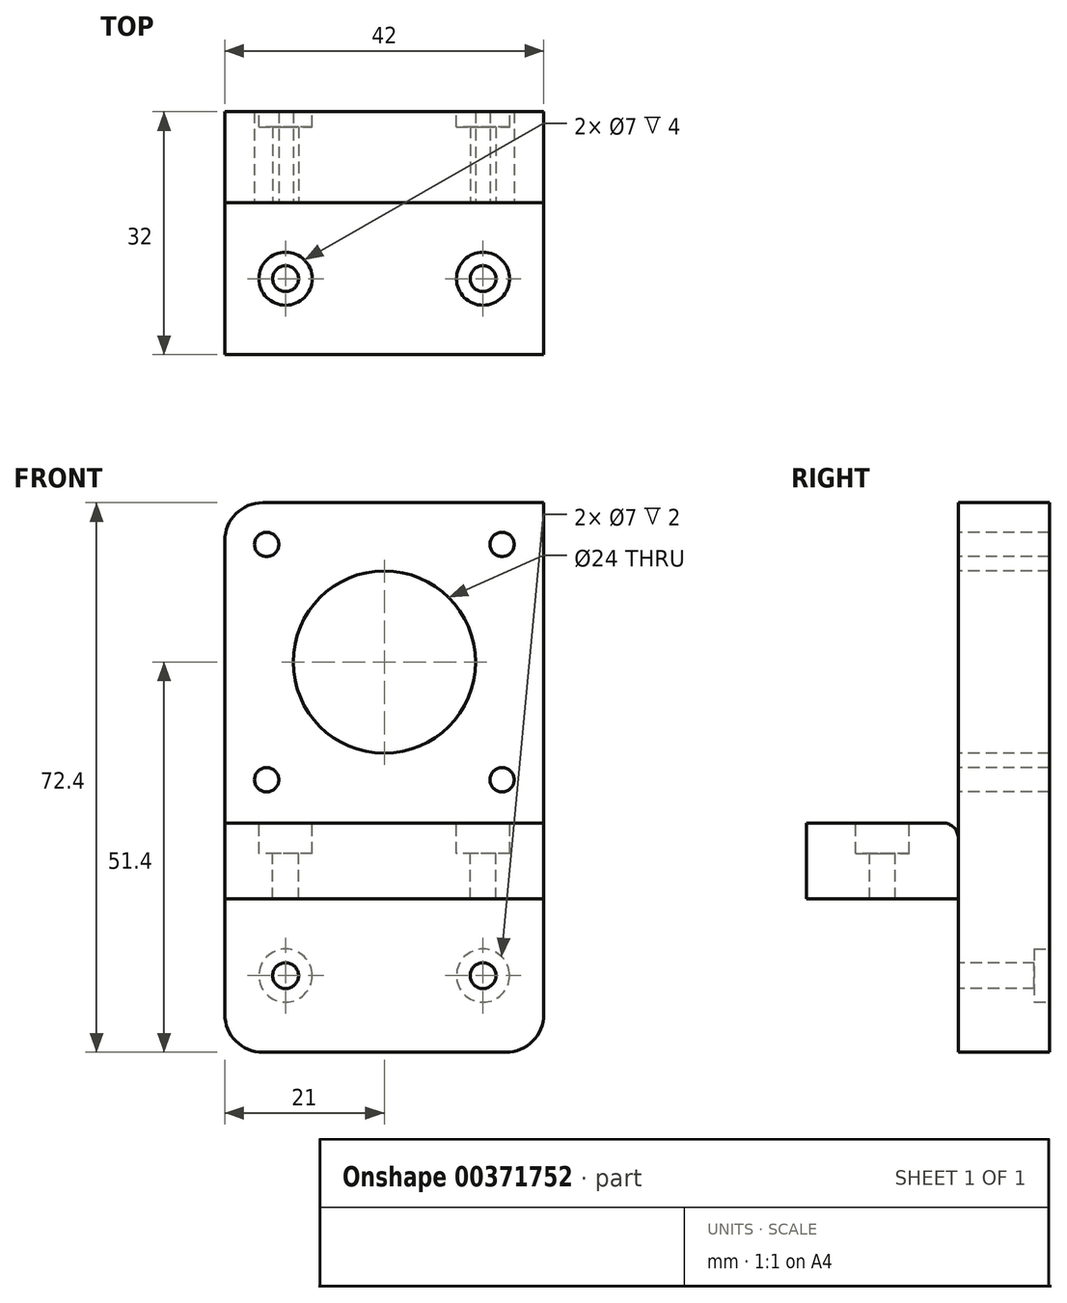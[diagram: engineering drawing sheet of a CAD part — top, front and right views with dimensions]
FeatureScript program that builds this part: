
annotation { "Feature Type Name" : "Feature", "Feature Type Description" : "" }
export const myFeature = defineFeature(function(context is Context, id is Id, definition is map)
    precondition{}
    {
        {
            var Q0;
            Q0=qCreatedBy(makeId("Front.planeOp"),FACE);
            var sketch = newSketch(context, id + "F0", { "sketchPlane" : qUnion([Q0])});
            skLineSegment(sketch, "E0.bottom", {"start": v(-21, 21) * mm, "end": v(21, 21) * mm});
            skLineSegment(sketch, "E0.left", {"start": v(-21, 21) * mm, "end": v(-21, -21) * mm});
            skLineSegment(sketch, "E0.right", {"start": v(21, 21) * mm, "end": v(21, -21) * mm});
            skPoint(sketch, "E0.middle", {"position": v(0, 0) * mm});
            skLineSegment(sketch, "E1", {"start": v(0, 0) * mm, "end": v(15.5, 0) * mm, "construction": true});
            skLineSegment(sketch, "E2", {"start": v(0, 0) * mm, "end": v(0, 15.5) * mm, "construction": true});
            skLineSegment(sketch, "E3", {"start": v(15.5, -21) * mm, "end": v(15.5, 21) * mm, "construction": true});
            skLineSegment(sketch, "E4", {"start": v(21, 15.5) * mm, "end": v(-21, 15.5) * mm, "construction": true});
            skLineSegment(sketch, "E5", {"start": v(0, 0) * mm, "end": v(-15.5, 0) * mm, "construction": true});
            skLineSegment(sketch, "E6", {"start": v(0, 0) * mm, "end": v(0, -15.5) * mm, "construction": true});
            skLineSegment(sketch, "E7", {"start": v(-15.5, 21) * mm, "end": v(-15.5, -21) * mm, "construction": true});
            skLineSegment(sketch, "E8", {"start": v(21, -15.5) * mm, "end": v(-21, -15.5) * mm, "construction": true});
            skCircle(sketch, "E9", {"center": v(-15.5, 15.5) * mm, "radius": 1.6 * mm});
            skCircle(sketch, "E10", {"center": v(15.5, 15.5) * mm, "radius": 1.6 * mm});
            skCircle(sketch, "E11", {"center": v(15.5, -15.5) * mm, "radius": 1.6 * mm});
            skCircle(sketch, "E12", {"center": v(-15.5, -15.5) * mm, "radius": 1.6 * mm});
            skLineSegment(sketch, "E13", {"start": v(-21, -21) * mm, "end": v(21, -21) * mm});
            skLineSegment(sketch, "E14.0", {"start": v(-21, -21.2) * mm, "end": v(21, -21.2) * mm});
            skLineSegment(sketch, "E15", {"start": v(21, -21.2) * mm, "end": v(21, -31.2) * mm});
            skLineSegment(sketch, "E16", {"start": v(-21, -31.2) * mm, "end": v(21, -31.2) * mm});
            skLineSegment(sketch, "E17.bottom", {"start": v(-21.2, 21) * mm, "end": v(21, 21) * mm});
            skLineSegment(sketch, "E17.right", {"start": v(21, 21) * mm, "end": v(21, -31.2) * mm});
            skCircle(sketch, "E18", {"center": v(0, 0) * mm, "radius": 12 * mm});
            skLineSegment(sketch, "E19.top", {"start": v(21, -51.4) * mm, "end": v(-21, -51.4) * mm});
            skLineSegment(sketch, "E19.left", {"start": v(21, -31.2) * mm, "end": v(21, -51.4) * mm});
            skLineSegment(sketch, "E20", {"start": v(21, -31.2) * mm, "end": v(21, -31.4) * mm, "construction": true});
            skLineSegment(sketch, "E21", {"start": v(21, -31.4) * mm, "end": v(-21, -31.4) * mm, "construction": true});
            skLineSegment(sketch, "E22", {"start": v(0, -41.3) * mm, "end": v(13, -41.3) * mm, "construction": true});
            skPoint(sketch, "E22.startSnap0", {"position": v(21, -41.3) * mm});
            skLineSegment(sketch, "E23", {"start": v(0, -41.3) * mm, "end": v(-13, -41.3) * mm, "construction": true});
            skCircle(sketch, "E24", {"center": v(13, -41.3) * mm, "radius": 1.7 * mm});
            skCircle(sketch, "E25", {"center": v(-13, -41.3) * mm, "radius": 1.7 * mm});
            skCircle(sketch, "E26", {"center": v(13, -41.3) * mm, "radius": 3.5 * mm});
            skCircle(sketch, "E27", {"center": v(-13, -41.3) * mm, "radius": 3.5 * mm});
            skLineSegment(sketch, "E28", {"start": v(-21, -21) * mm, "end": v(-21, -51.4) * mm});
            skSolve(sketch);
        }
        {
            var Q0;
            {var subQ4=sQuery(id+"F0.wireOp",EDGE,"E14.0");Q0=makeQuery(id+"F0.imprint","IMPRINT",FACE,{"disambiguationData":[TD([[makeQuery(id+"F0.imprint","IMPRINT",EDGE,{"derivedFrom":subQ4}),-1.0]])]});}
            extrude(context, id + "F1", {"entities" : qUnion([Q0]), "depth" : 20 * mm});
        }
        {
            var Q0;
            {var subQ3=sQuery(id+"F0.wireOp",EDGE,"E0.left");Q0=makeQuery(id+"F0.imprint","IMPRINT",FACE,{"disambiguationData":[TD([[makeQuery(id+"F0.imprint","IMPRINT",EDGE,{"derivedFrom":subQ3}),-1.0]])]});}
            var Q1;
            {var subQ4=sQuery(id+"F0.wireOp",EDGE,"E14.0");Q1=makeQuery(id+"F0.imprint","IMPRINT",FACE,{"disambiguationData":[TD([[makeQuery(id+"F0.imprint","IMPRINT",EDGE,{"derivedFrom":subQ4}),-1.0]])]});}
            var Q2;
            {var subQ4=sQuery(id+"F0.wireOp",EDGE,"E0.left");Q2=makeQuery(id+"F0.imprint","IMPRINT",FACE,{"disambiguationData":[TD([[makeQuery(id+"F0.imprint","IMPRINT",EDGE,{"derivedFrom":subQ4}),1.0]])]});}
            var Q3;
            {var subQ1=sQuery(id+"F0.wireOp",EDGE,"E16");Q3=makeQuery(id+"F0.imprint","IMPRINT",FACE,{"disambiguationData":[TD([[makeQuery(id+"F0.imprint","IMPRINT",EDGE,{"derivedFrom":subQ1}),-1.0]])]});}
            var Q4;
            {var subQ0=sQuery(id+"F0.wireOp",EDGE,"E13");Q4=makeQuery(id+"F0.imprint","IMPRINT",FACE,{"disambiguationData":[TD([[makeQuery(id+"F0.imprint","IMPRINT",EDGE,{"derivedFrom":subQ0}),-1.0]])]});}
            extrude(context, id + "F2", {"entities" : qUnion([Q0, Q1, Q2, Q3, Q4]), "oppositeDirection" : true, "depth" : 12 * mm});
        }
        {
            var Q0;
            Q0=makeQuery(id+"F1.opExtrude","SWEPT_FACE",FACE,{"disambiguationData":[OSD([sQuery(id+"F0.wireOp",EDGE,"E14.0")])]});
            var sketch = newSketch(context, id + "F3", { "sketchPlane" : qUnion([Q0])});
            skLineSegment(sketch, "E29", {"start": v(0, 0) * mm, "end": v(0, -20) * mm, "construction": true});
            skLineSegment(sketch, "E30", {"start": v(0, -10) * mm, "end": v(13, -10) * mm, "construction": true});
            skPoint(sketch, "E30.endSnap0", {"position": v(0, -10) * mm});
            skLineSegment(sketch, "E31", {"start": v(0, -10) * mm, "end": v(-13, -10) * mm, "construction": true});
            skCircle(sketch, "E32", {"center": v(-13, -10) * mm, "radius": 1.7 * mm});
            skCircle(sketch, "E33", {"center": v(13, -10) * mm, "radius": 1.7 * mm});
            skCircle(sketch, "E34", {"center": v(-13, -10) * mm, "radius": 3.5 * mm});
            skCircle(sketch, "E35", {"center": v(13, -10) * mm, "radius": 3.5 * mm});
            skSolve(sketch);
        }
        {
            var Q0;
            Q0=makeQuery(id+"F3.imprint","IMPRINT",FACE,{"disambiguationData":[TD([[makeQuery(id+"F3.imprint","IMPRINT",EDGE,{"derivedFrom":sQuery(id+"F3.wireOp",EDGE,"E32")}),1.0]])]});
            var Q1;
            Q1=makeQuery(id+"F3.imprint","IMPRINT",FACE,{"disambiguationData":[TD([[makeQuery(id+"F3.imprint","IMPRINT",EDGE,{"derivedFrom":sQuery(id+"F3.wireOp",EDGE,"E33")}),1.0]])]});
            extrude(context, id + "F4", {"entities" : qUnion([Q0, Q1]), "operationType" : NewBodyOperationType.REMOVE, "oppositeDirection" : true, "depth" : 25 * mm});
        }
        {
            var Q0;
            Q0=makeQuery(id+"F3.imprint","IMPRINT",FACE,{"disambiguationData":[TD([[makeQuery(id+"F3.imprint","IMPRINT",EDGE,{"derivedFrom":sQuery(id+"F3.wireOp",EDGE,"E32")}),-1.0]])]});
            var Q1;
            Q1=makeQuery(id+"F3.imprint","IMPRINT",FACE,{"disambiguationData":[TD([[makeQuery(id+"F3.imprint","IMPRINT",EDGE,{"derivedFrom":sQuery(id+"F3.wireOp",EDGE,"E33")}),-1.0]])]});
            extrude(context, id + "F5", {"entities" : qUnion([Q0, Q1]), "operationType" : NewBodyOperationType.REMOVE, "oppositeDirection" : true, "depth" : 4 * mm});
        }
        {
            var Q0;
            Q0=makeQuery(id+"F0.imprint","IMPRINT",FACE,{"disambiguationData":[TD([[makeQuery(id+"F0.imprint","IMPRINT",EDGE,{"derivedFrom":sQuery(id+"F0.wireOp",EDGE,"E19.bottom")}),1.0]])]});
            var Q1;
            Q1=makeQuery(id+"F0.imprint","IMPRINT",FACE,{"disambiguationData":[TD([[makeQuery(id+"F0.imprint","IMPRINT",EDGE,{"derivedFrom":sQuery(id+"F0.wireOp",EDGE,"E24")}),-1.0]])]});
            var Q2;
            Q2=makeQuery(id+"F0.imprint","IMPRINT",FACE,{"disambiguationData":[TD([[makeQuery(id+"F0.imprint","IMPRINT",EDGE,{"derivedFrom":sQuery(id+"F0.wireOp",EDGE,"E25")}),-1.0]])]});
            extrude(context, id + "F6", {"entities" : qUnion([Q0, Q1, Q2]), "operationType" : NewBodyOperationType.ADD, "oppositeDirection" : true, "depth" : 12 * mm});
        }
        {
            var Q0;
            {var subQ0=sQuery(id+"F0.wireOp",EDGE,"E19.bottom");Q0=makeQuery(id+"F6.boolean.opBoolean","MERGE",FACE,{"derivedFrom":[makeQuery(id+"F2.opExtrude","CAP_FACE",FACE,{"disambiguationData":[OSD([sQuery(id+"F0.wireOp",EDGE,"E9"),sQuery(id+"F0.wireOp",EDGE,"E10"),sQuery(id+"F0.wireOp",EDGE,"E11"),sQuery(id+"F0.wireOp",EDGE,"E12"),sQuery(id+"F0.wireOp",EDGE,"E17.bottom"),sQuery(id+"F0.wireOp",EDGE,"E17.top"),sQuery(id+"F0.wireOp",EDGE,"E17.left"),sQuery(id+"F0.wireOp",EDGE,"E17.right"),sQuery(id+"F0.wireOp",EDGE,"E18"),subQ0])],"isStart":false}),makeQuery(id+"F6.opExtrude","CAP_FACE",FACE,{"disambiguationData":[OSD([subQ0,sQuery(id+"F0.wireOp",EDGE,"E19.top"),sQuery(id+"F0.wireOp",EDGE,"E19.left"),sQuery(id+"F0.wireOp",EDGE,"E19.right"),sQuery(id+"F0.wireOp",EDGE,"E24"),sQuery(id+"F0.wireOp",EDGE,"E25")])],"isStart":false})]});}
            var sketch = newSketch(context, id + "F7", { "sketchPlane" : qUnion([Q0])});
            skCircle(sketch, "E36", {"center": v(-13, -41.3) * mm, "radius": 3.5 * mm});
            skCircle(sketch, "E37", {"center": v(13, -41.3) * mm, "radius": 3.5 * mm});
            skSolve(sketch);
        }
        {
            var Q0;
            Q0=makeQuery(id+"F7.imprint","IMPRINT",FACE,{"disambiguationData":[TD([[makeQuery(id+"F7.imprint","IMPRINT",EDGE,{"derivedFrom":sQuery(id+"F7.wireOp",EDGE,"E36")}),1.0]])]});
            var Q1;
            Q1=makeQuery(id+"F7.imprint","IMPRINT",FACE,{"disambiguationData":[TD([[makeQuery(id+"F7.imprint","IMPRINT",EDGE,{"derivedFrom":sQuery(id+"F7.wireOp",EDGE,"E37")}),1.0]])]});
            extrude(context, id + "F8", {"entities" : qUnion([Q0, Q1]), "operationType" : NewBodyOperationType.REMOVE, "oppositeDirection" : true, "depth" : 2 * mm});
        }
        {
            var Q0;
            Q0=makeQuery(id+"F2.opExtrude","SWEPT_EDGE",EDGE,{"disambiguationData":[OSD([sQuery(id+"F0.wireOp",EDGE,"E17.bottom"),sQuery(id+"F0.wireOp",EDGE,"E17.right")])]});
            var Q1;
            Q1=makeQuery(id+"F2.opExtrude","SWEPT_EDGE",EDGE,{"disambiguationData":[OSD([sQuery(id+"F0.wireOp",EDGE,"E0.left"),sQuery(id+"F0.wireOp",EDGE,"E17.bottom")])]});
            var Q2;
            Q2=makeQuery(id+"F2.opExtrude","SWEPT_EDGE",EDGE,{"disambiguationData":[OSD([sQuery(id+"F0.wireOp",EDGE,"E19.top"),sQuery(id+"F0.wireOp",EDGE,"E28")])]});
            var Q3;
            Q3=makeQuery(id+"F2.opExtrude","SWEPT_EDGE",EDGE,{"disambiguationData":[OSD([sQuery(id+"F0.wireOp",EDGE,"E19.top"),sQuery(id+"F0.wireOp",EDGE,"E19.left")])]});
            fillet(context, id + "F9", {"entities" : qUnion([Q0, Q1, Q2, Q3]), "radius" : 5 * mm, "tangentPropagation" : true, "allowEdgeOverflow" : false});
        }
        {
            var Q0;
            Q0=makeQuery(id+"F1.opExtrude","CAP_EDGE",EDGE,{"disambiguationData":[OSD([sQuery(id+"F0.wireOp",EDGE,"E14.0")])],"isStart":true});
            fillet(context, id + "F10", {"entities" : qUnion([Q0]), "radius" : 2 * mm, "tangentPropagation" : true, "allowEdgeOverflow" : false});
        }
    });
